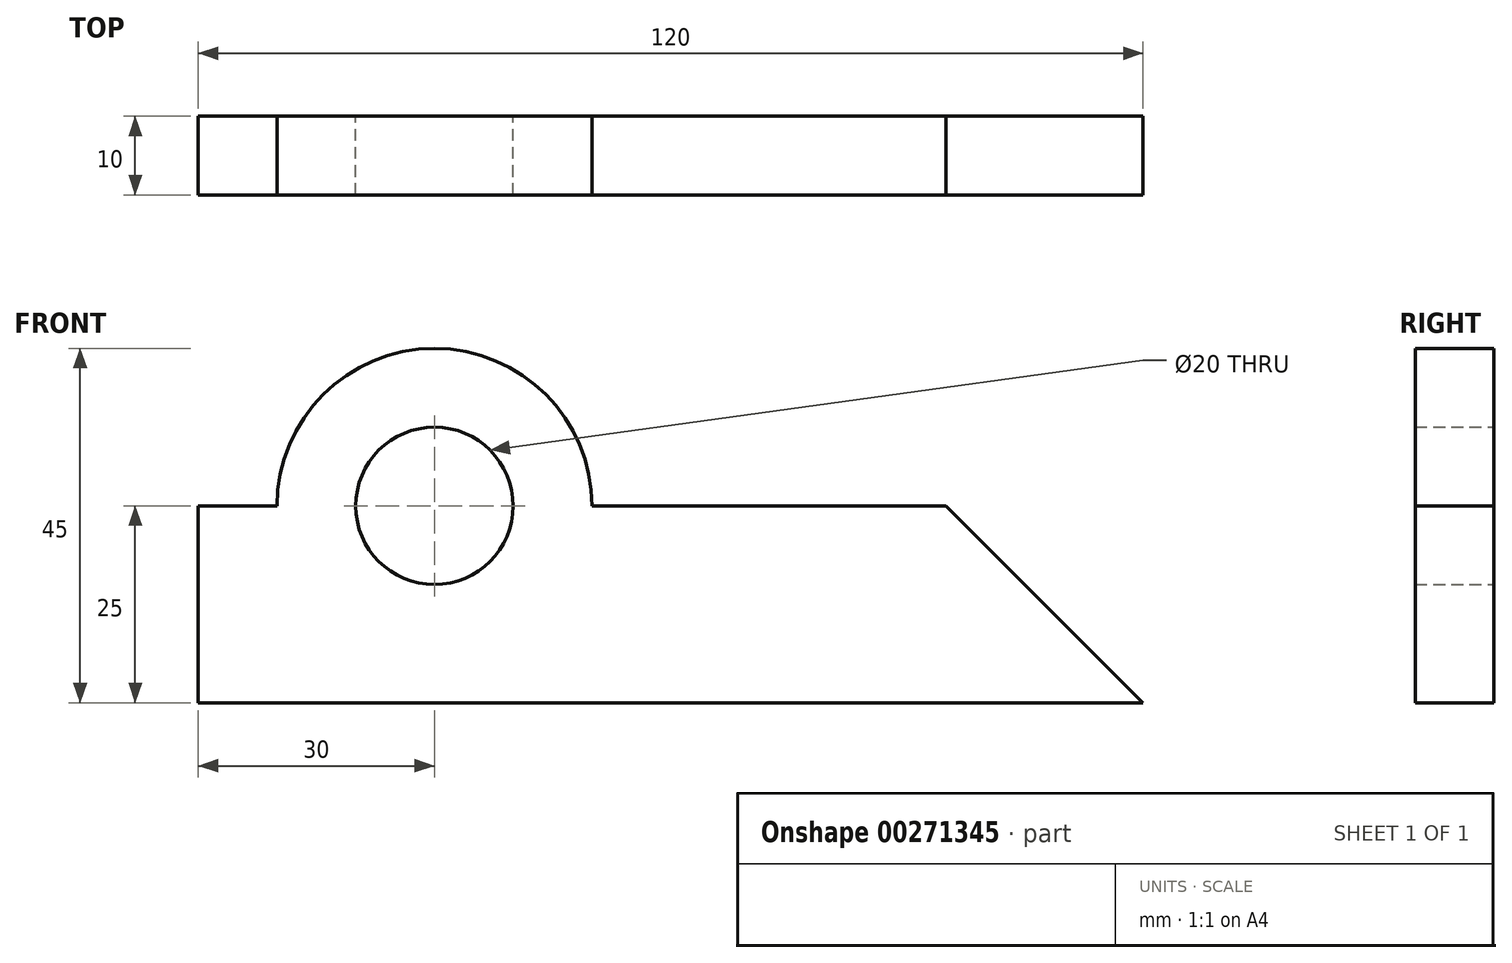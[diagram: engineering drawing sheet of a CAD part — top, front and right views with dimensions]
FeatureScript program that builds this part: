
annotation { "Feature Type Name" : "Feature", "Feature Type Description" : "" }
export const myFeature = defineFeature(function(context is Context, id is Id, definition is map)
    precondition{}
    {
        {
            var Q0;
            Q0=qCreatedBy(makeId("Front.planeOp"),FACE);
            var sketch = newSketch(context, id + "F0", { "sketchPlane" : qUnion([Q0])});
            skLineSegment(sketch, "E0", {"start": v(0, 0) * mm, "end": v(120, 0) * mm});
            skLineSegment(sketch, "E1", {"start": v(0, 0) * mm, "end": v(0, 25) * mm});
            skLineSegment(sketch, "E2", {"start": v(0, 25) * mm, "end": v(10, 25) * mm});
            skLineSegment(sketch, "E3", {"start": v(50, 25) * mm, "end": v(95, 25) * mm});
            skLineSegment(sketch, "E4", {"start": v(95, 25) * mm, "end": v(120, 0) * mm});
            skCircle(sketch, "E5", {"center": v(30, 25) * mm, "radius": 10 * mm});
            skArc(sketch, "E6", {"start": v(50, 25) * mm, "mid": v(30, 45) * mm, "end": v(10, 25) * mm});
            skSolve(sketch);
        }
        {
            var Q0;
            Q0 = qSketchRegion(id + "F0", true);
            extrude(context, id + "F1", {"entities" : qUnion([Q0]), "depth" : 10 * mm});
        }
    });
